# Revit family: 0030314
name_source: partatom
category: Lighting Fixtures
revit_build: Autodesk Revit 2016 (Build: 20150220_1215(x64)
units: mm (PartAtom-declared; Revit-internal decimal feet)

## family parameters
Cut with Voids When Loaded = No
Host = Face
Light Source = Yes
OmniClass Number = 23.80.70.00
OmniClass Title = Lighting
Part Type = Normal
Room Calculation Point = No
Round Connector Dimension = Use Diameter
Shared = No

## types (2) — shared parameters
Assembly Code = D5020200
AssetType = Fixed
ClassificationName = Uniclass2015
ClassificationValue = EF_70_80
Color Filter = 16777215
Default Elevation = 1219 mm
DiameterRecess_SYL = 191 mm  [stored 0.62664 ft]
DiameterTop_SYL = 134 mm  [stored 0.439633 ft]
Diameter_SYL = 220 mm  [stored 0.721785 ft]
Dimming Lamp Color Temperature Shift = <None>
DocumentationLiterature = http://www.sylvania-lighting.com
DurationUnit = hours
ElectricShockClassification = Class II
Emit Shape Visible in Rendering = No
Emit from Rectangle Length = 180 mm  [stored 0.590551 ft]
Emit from Rectangle Width = 180 mm  [stored 0.590551 ft]
ExpectedLife = 50000
HeightBezel_SYL = 3 mm  [stored 0.00984252 ft]
Height_SYL = 61 mm  [stored 0.200131 ft]
IfcExportAs = IfcLightFixtureType
IfcExportType = IfcLightFixtureType
ImpactProtectionIndex = IK07
IngressProtection = IP40/20
InputNominalFrequency = 50/60 Hz
InputVoltage = AC 220-240 V
Keynote = 16500
Lamp = LED
LampColourRenderingIndex = 80
LampColourTemperature = 3000 K
LampMacAdamStep = 5
LampsType = LED
Manufacturer = Feilo Sylvania
ManufacturerName = Feilo Sylvania
Material = aluminium housing, na diffuser
Material_1_FEILO = Trim-Sylvania-STARTDownlight-White
Material_2_FEILO = Diffuser-Sylvania-STARTDownlight
Material_3_FEILO = Top-Sylvania-STARTDownlight
Material_4_FEILO = Reflector-Sylvania-STARTDownlight
Model = Insaver Slim Square UGR19 IP44 200 2250lm 830
ModelNumber = 0030314
ModelReference = Insaver Slim Square UGR19 IP44 200 2250lm 830
Name = Insaver Slim Square UGR19 IP44 200 2250lm 830
NominalDepth = 217 mm  [stored 0.711942 ft]
NominalHeight = 60 mm  [stored 0.19685 ft]
NominalLength = 217 mm  [stored 0.711942 ft]
PowerFactor = 0.9
SizeSq1_SYL = No
Tilt Angle = -90.00°
Type Image = <None>
TypeName = Insaver Slim Square UGR19 IP44 200 2250lm 830
URL = http://www.sylvania-lighting.com
Voltage = 230 V
Weight = 9.84 kg
WidthDiffuser_SYL = 180 mm  [stored 0.590551 ft]
WidthLED_SYL = 30 mm  [stored 0.0984252 ft]
zero-valued in all types: Cost

## per-type parameters (varying)
| type | Apparent Load | LampNominalLuminous | LuminousEfficacy | Photometric Web File | PowerConsumption |
| 0030314 Insaver Slim S UGR19 IP44 200 2250lm 830 | 20 VA | 2250 lm | 113 lm/W | 0030314.ies | 20 W |
| 0030314 Insaver Slim S UGR19 IP44 200 2250lm 830 Emergency mode | 23 VA | 384 lm | 16.7 lm/W | 0030314EM.ies | 23 W |

note: [stored X ft] marks values corroborated as IEEE doubles in the binary element streams (Revit-internal decimal feet)

## geometry (parser evidence)
native form markers: Sweep x2
no freeform markers — native parametric forms only
